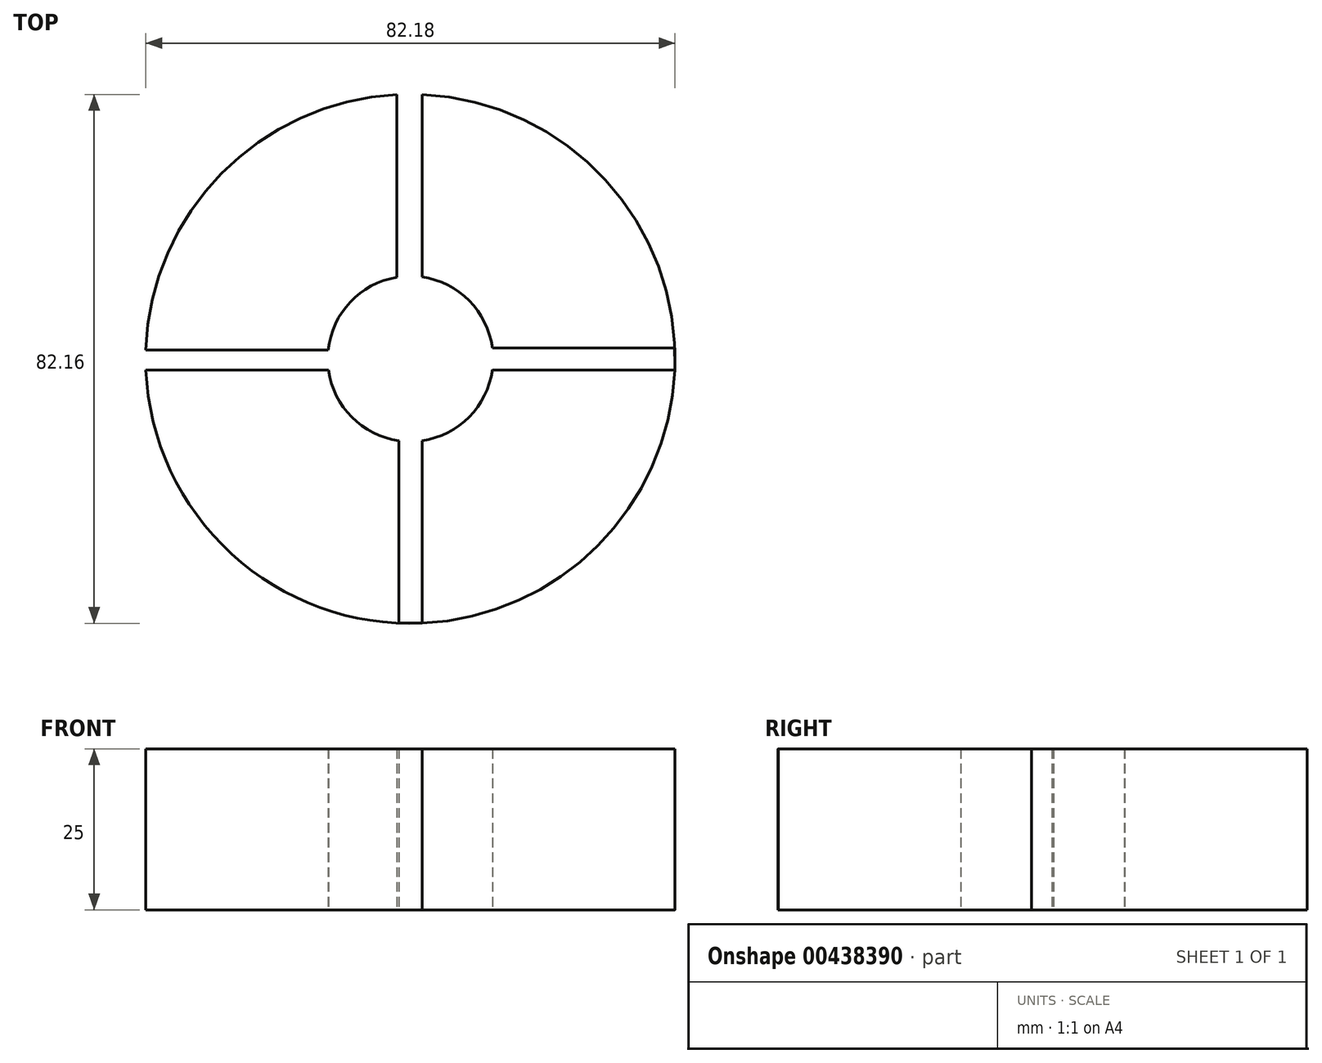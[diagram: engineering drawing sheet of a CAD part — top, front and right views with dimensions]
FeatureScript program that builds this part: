
annotation { "Feature Type Name" : "Feature", "Feature Type Description" : "" }
export const myFeature = defineFeature(function(context is Context, id is Id, definition is map)
    precondition{}
    {
        {
            var Q0;
            Q0=qCreatedBy(makeId("Top.planeOp"),FACE);
            var sketch = newSketch(context, id + "F0", { "sketchPlane" : qUnion([Q0])});
            skCircle(sketch, "E0", {"center": v(0, 0) * mm, "radius": 41.1 * mm});
            skCircle(sketch, "E1", {"center": v(0, 0) * mm, "radius": 12.84 * mm});
            skLineSegment(sketch, "E2.bottom", {"start": v(-41.08, 1.4) * mm, "end": v(-12.72, 1.4) * mm});
            skLineSegment(sketch, "E2.top", {"start": v(-41.08, -1.74) * mm, "end": v(-12.72, -1.74) * mm});
            skLineSegment(sketch, "E2.left", {"start": v(-41.08, 1.4) * mm, "end": v(-41.08, -1.74) * mm});
            skLineSegment(sketch, "E2.right", {"start": v(-12.72, 1.4) * mm, "end": v(-12.72, -1.74) * mm});
            skLineSegment(sketch, "E3.bottom", {"start": v(-1.8, -12.71) * mm, "end": v(1.82, -12.71) * mm});
            skLineSegment(sketch, "E3.top", {"start": v(-1.8, -41.06) * mm, "end": v(1.82, -41.06) * mm});
            skLineSegment(sketch, "E3.left", {"start": v(-1.8, -12.71) * mm, "end": v(-1.8, -41.06) * mm});
            skLineSegment(sketch, "E3.right", {"start": v(1.82, -12.71) * mm, "end": v(1.82, -41.06) * mm});
            skLineSegment(sketch, "E4.bottom", {"start": v(12.73, 1.7) * mm, "end": v(41.07, 1.7) * mm});
            skLineSegment(sketch, "E4.top", {"start": v(12.73, -1.74) * mm, "end": v(41.07, -1.74) * mm});
            skLineSegment(sketch, "E4.left", {"start": v(12.73, 1.7) * mm, "end": v(12.73, -1.74) * mm});
            skLineSegment(sketch, "E4.right", {"start": v(41.07, 1.7) * mm, "end": v(41.07, -1.74) * mm});
            skLineSegment(sketch, "E5.bottom", {"start": v(-2.11, 12.66) * mm, "end": v(1.8, 12.66) * mm});
            skLineSegment(sketch, "E5.top", {"start": v(-2.11, 41.06) * mm, "end": v(1.8, 41.06) * mm});
            skLineSegment(sketch, "E5.left", {"start": v(-2.11, 12.66) * mm, "end": v(-2.11, 41.06) * mm});
            skLineSegment(sketch, "E5.right", {"start": v(1.8, 12.66) * mm, "end": v(1.8, 41.06) * mm});
            skSolve(sketch);
        }
        {
            var Q0;
            {var subQ6=sQuery(id+"F0.wireOp",EDGE,"E3.top");Q0=makeQuery(id+"F0.imprint","IMPRINT",FACE,{"disambiguationData":[TD([[makeQuery(id+"F0.imprint","IMPRINT",EDGE,{"derivedFrom":subQ6}),-1.0]])]});}
            var Q1;
            {var subQ0=sQuery(id+"F0.wireOp",EDGE,"E3.right");Q1=makeQuery(id+"F0.imprint","IMPRINT",FACE,{"disambiguationData":[TD([[makeQuery(id+"F0.imprint","IMPRINT",EDGE,{"derivedFrom":subQ0}),1.0]])]});}
            var Q2;
            {var subQ0=sQuery(id+"F0.wireOp",EDGE,"E4.bottom");Q2=makeQuery(id+"F0.imprint","IMPRINT",FACE,{"disambiguationData":[TD([[makeQuery(id+"F0.imprint","IMPRINT",EDGE,{"derivedFrom":subQ0}),1.0]])]});}
            var Q3;
            {var subQ1=sQuery(id+"F0.wireOp",EDGE,"E0");var subQ3=sQuery(id+"F0.wireOp",EDGE,"E5.left");var subQ4=makeQuery(id+"F0.imprint","INTERSECT",VERTEX,{"derivedFrom":[subQ1,subQ3]});Q3=makeQuery(id+"F0.imprint","IMPRINT",FACE,{"disambiguationData":[TD([[makeQuery(id+"F0.imprint","IMPRINT",EDGE,{"disambiguationData":[TD([[subQ4,-1.0]])],"derivedFrom":subQ1}),1.0]])]});}
            extrude(context, id + "F1", {"entities" : qUnion([Q0, Q1, Q2, Q3]), "depth" : 25 * mm});
        }
    });
